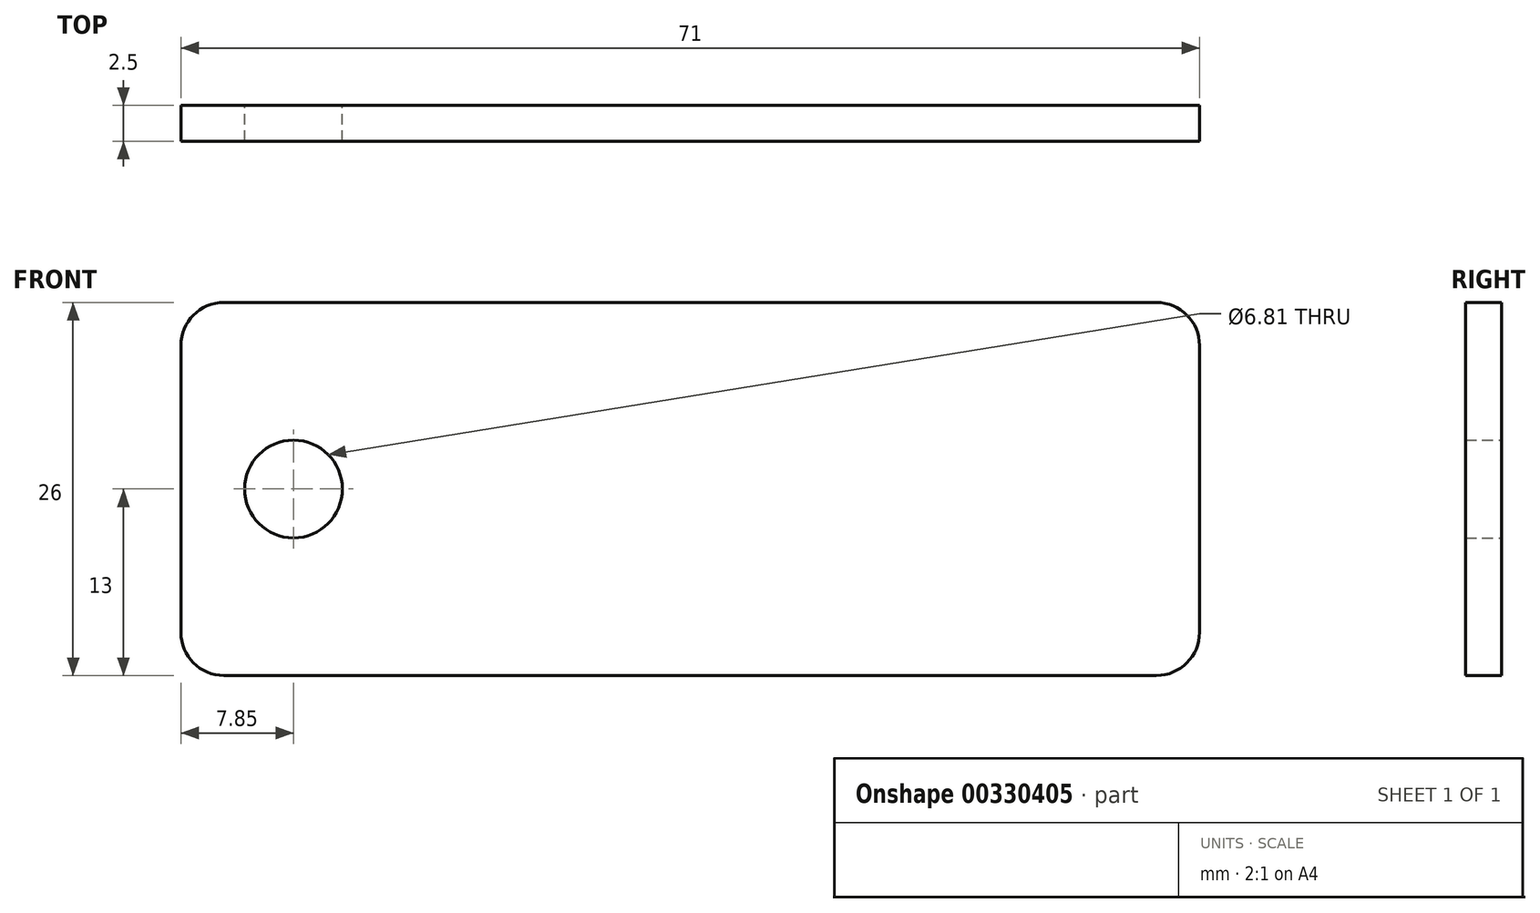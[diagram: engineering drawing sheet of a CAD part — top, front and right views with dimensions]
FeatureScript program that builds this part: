
annotation { "Feature Type Name" : "Feature", "Feature Type Description" : "" }
export const myFeature = defineFeature(function(context is Context, id is Id, definition is map)
    precondition{}
    {
        {
            var Q0;
            Q0=qCreatedBy(makeId("Front.planeOp"),FACE);
            var sketch = newSketch(context, id + "F0", { "sketchPlane" : qUnion([Q0])});
            skLineSegment(sketch, "E0.bottom", {"start": v(-4.85, 13) * mm, "end": v(60.15, 13) * mm});
            skLineSegment(sketch, "E0.top", {"start": v(-4.85, -13) * mm, "end": v(60.15, -13) * mm});
            skLineSegment(sketch, "E0.left", {"start": v(-7.85, 10) * mm, "end": v(-7.85, -10) * mm});
            skLineSegment(sketch, "E0.right", {"start": v(63.15, 10) * mm, "end": v(63.15, -10) * mm});
            skPoint(sketch, "E1.visualSharp", {"position": v(-7.85, 13) * mm});
            skArc(sketch, "E1.filletArc", {"start": v(-4.85, 13) * mm, "mid": v(-6.97, 12.12) * mm, "end": v(-7.85, 10) * mm});
            skPoint(sketch, "E2.visualSharp", {"position": v(-7.85, -13) * mm});
            skArc(sketch, "E2.filletArc", {"start": v(-7.85, -10) * mm, "mid": v(-6.97, -12.12) * mm, "end": v(-4.85, -13) * mm});
            skPoint(sketch, "E3.visualSharp", {"position": v(63.15, -13) * mm});
            skArc(sketch, "E3.filletArc", {"start": v(60.15, -13) * mm, "mid": v(62.27, -12.12) * mm, "end": v(63.15, -10) * mm});
            skPoint(sketch, "E4.visualSharp", {"position": v(63.15, 13) * mm});
            skArc(sketch, "E4.filletArc", {"start": v(63.15, 10) * mm, "mid": v(62.27, 12.12) * mm, "end": v(60.15, 13) * mm});
            skCircle(sketch, "E5", {"center": v(0, 0) * mm, "radius": 3.4 * mm});
            skPoint(sketch, "E6", {"position": v(63.15, 0) * mm});
            skSolve(sketch);
        }
        {
            var Q0;
            Q0 = qSketchRegion(id + "F0", true);
            var Q1;
            Q1=makeQuery(id+"F0.imprint","IMPRINT",FACE,{"disambiguationData":[TD([[makeQuery(id+"F0.imprint","IMPRINT",EDGE,{"derivedFrom":sQuery(id+"F0.wireOp",EDGE,"E0.bottom")}),-1.0]])]});
            extrude(context, id + "F1", {"entities" : qUnion([Q0, Q1]), "depth" : 2.5 * mm, "offsetDistance" : 25 * mm});
        }
    });
